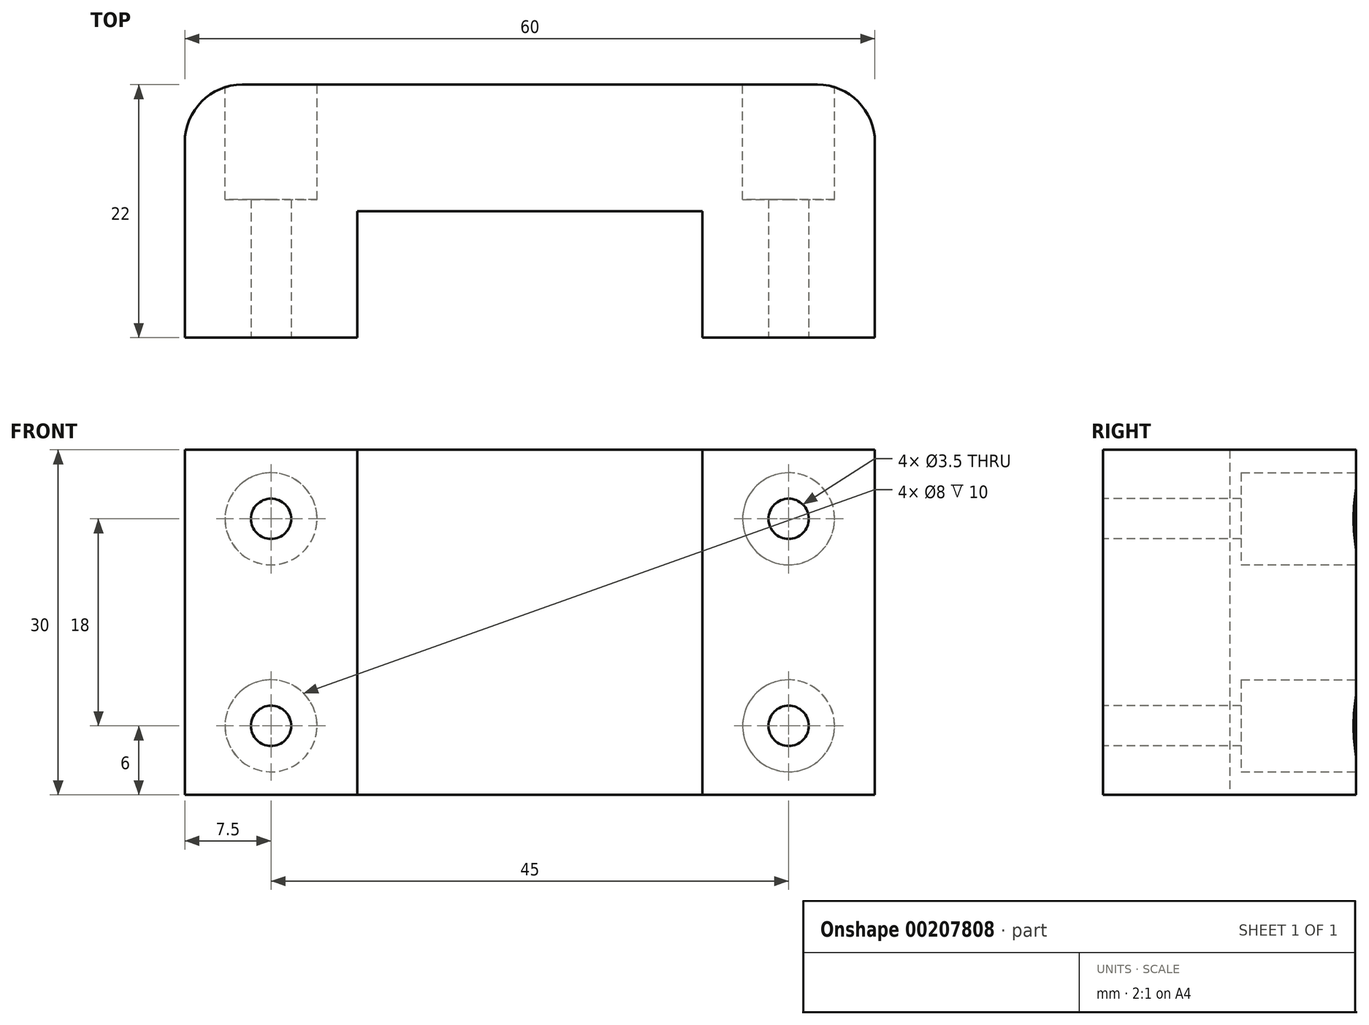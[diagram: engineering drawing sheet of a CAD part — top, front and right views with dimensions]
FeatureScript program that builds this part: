
annotation { "Feature Type Name" : "Feature", "Feature Type Description" : "" }
export const myFeature = defineFeature(function(context is Context, id is Id, definition is map)
    precondition{}
    {
        {
            var Q0;
            Q0=qCreatedBy(makeId("Top.planeOp"),FACE);
            var sketch = newSketch(context, id + "F0", { "sketchPlane" : qUnion([Q0])});
            skLineSegment(sketch, "E0.bottom", {"start": v(-25, 22) * mm, "end": v(25, 22) * mm});
            skLineSegment(sketch, "E0.top", {"start": v(-30, 0) * mm, "end": v(30, 0) * mm});
            skLineSegment(sketch, "E0.left", {"start": v(-30, 17) * mm, "end": v(-30, 0) * mm});
            skLineSegment(sketch, "E0.right", {"start": v(30, 17) * mm, "end": v(30, 0) * mm});
            skLineSegment(sketch, "E1.bottom", {"start": v(-15, 11) * mm, "end": v(15, 11) * mm});
            skLineSegment(sketch, "E1.top", {"start": v(-15, -2) * mm, "end": v(15, -2) * mm});
            skLineSegment(sketch, "E1.left", {"start": v(-15, 11) * mm, "end": v(-15, -2) * mm});
            skLineSegment(sketch, "E1.right", {"start": v(15, 11) * mm, "end": v(15, -2) * mm});
            skPoint(sketch, "E2.visualSharp", {"position": v(30, 22) * mm});
            skArc(sketch, "E2.filletArc", {"start": v(30, 17) * mm, "mid": v(28.54, 20.54) * mm, "end": v(25, 22) * mm});
            skPoint(sketch, "E3.visualSharp", {"position": v(-30, 22) * mm});
            skArc(sketch, "E3.filletArc", {"start": v(-25, 22) * mm, "mid": v(-28.54, 20.54) * mm, "end": v(-30, 17) * mm});
            skSolve(sketch);
        }
        {
            var Q0;
            Q0=makeQuery(id+"F0.imprint","IMPRINT",FACE,{"disambiguationData":[TD([[makeQuery(id+"F0.imprint","IMPRINT",EDGE,{"derivedFrom":sQuery(id+"F0.wireOp",EDGE,"E0.bottom")}),-1.0]])]});
            extrude(context, id + "F1", {"entities" : qUnion([Q0]), "depth" : 30 * mm});
        }
        {
            var Q0;
            {var subQ0=sQuery(id+"F0.wireOp",EDGE,"E0.top");Q0=makeQuery(id+"F1.opExtrude","SWEPT_FACE",FACE,{"disambiguationData":[OSD([subQ0]),TDD([makeQuery(id+"F0.imprint","IMPRINT",EDGE,{"disambiguationData":[TD([[makeQuery(id+"F0.imprint","INTERSECT",VERTEX,{"derivedFrom":[subQ0,sQuery(id+"F0.wireOp",EDGE,"E0.left")]}),-1.0]])],"derivedFrom":subQ0})])]});}
            var sketch = newSketch(context, id + "F2", { "sketchPlane" : qUnion([Q0])});
            skCircle(sketch, "E4", {"center": v(-22.5, 24) * mm, "radius": 1.75 * mm});
            skCircle(sketch, "E5", {"center": v(-22.5, 6) * mm, "radius": 1.75 * mm});
            skSolve(sketch);
        }
        {
            var Q0;
            {var subQ0=sQuery(id+"F0.wireOp",EDGE,"E0.top");Q0=makeQuery(id+"F1.opExtrude","SWEPT_FACE",FACE,{"disambiguationData":[OSD([subQ0]),TDD([makeQuery(id+"F0.imprint","IMPRINT",EDGE,{"disambiguationData":[TD([[makeQuery(id+"F0.imprint","INTERSECT",VERTEX,{"derivedFrom":[subQ0,sQuery(id+"F0.wireOp",EDGE,"E0.right")]}),1.0]])],"derivedFrom":subQ0})])]});}
            var sketch = newSketch(context, id + "F3", { "sketchPlane" : qUnion([Q0])});
            skCircle(sketch, "E6", {"center": v(22.5, 24) * mm, "radius": 1.75 * mm});
            skCircle(sketch, "E7", {"center": v(22.5, 6) * mm, "radius": 1.75 * mm});
            skSolve(sketch);
        }
        {
            var Q0;
            Q0=makeQuery(id+"F2.imprint","IMPRINT",FACE,{"disambiguationData":[TD([[makeQuery(id+"F2.imprint","IMPRINT",EDGE,{"derivedFrom":sQuery(id+"F2.wireOp",EDGE,"E4")}),1.0]])]});
            var Q1;
            Q1=makeQuery(id+"F2.imprint","IMPRINT",FACE,{"disambiguationData":[TD([[makeQuery(id+"F2.imprint","IMPRINT",EDGE,{"derivedFrom":sQuery(id+"F2.wireOp",EDGE,"E5")}),1.0]])]});
            var Q2;
            Q2=makeQuery(id+"F3.imprint","IMPRINT",FACE,{"disambiguationData":[TD([[makeQuery(id+"F3.imprint","IMPRINT",EDGE,{"derivedFrom":sQuery(id+"F3.wireOp",EDGE,"E7")}),1.0]])]});
            var Q3;
            Q3=makeQuery(id+"F3.imprint","IMPRINT",FACE,{"disambiguationData":[TD([[makeQuery(id+"F3.imprint","IMPRINT",EDGE,{"derivedFrom":sQuery(id+"F3.wireOp",EDGE,"E6")}),1.0]])]});
            extrude(context, id + "F4", {"entities" : qUnion([Q0, Q1, Q2, Q3]), "operationType" : NewBodyOperationType.REMOVE, "endBound" : BoundingType.THROUGH_ALL, "oppositeDirection" : true, "depth" : 25 * mm});
        }
        {
            var Q0;
            Q0=makeQuery(id+"F1.opExtrude","SWEPT_FACE",FACE,{"disambiguationData":[OSD([sQuery(id+"F0.wireOp",EDGE,"E0.bottom")])]});
            var sketch = newSketch(context, id + "F5", { "sketchPlane" : qUnion([Q0])});
            skCircle(sketch, "E8", {"center": v(22.5, 24) * mm, "radius": 4 * mm});
            skCircle(sketch, "E9", {"center": v(22.5, 6) * mm, "radius": 4 * mm});
            skCircle(sketch, "E10", {"center": v(-22.5, 24) * mm, "radius": 4 * mm});
            skCircle(sketch, "E11", {"center": v(-22.5, 6) * mm, "radius": 4 * mm});
            skSolve(sketch);
        }
        {
            var Q0;
            {var subQ0=sQuery(id+"F5.wireOp",EDGE,"E8");var subQ1=makeQuery(id+"F1.opExtrude","SWEPT_EDGE",EDGE,{"disambiguationData":[OSD([sQuery(id+"F0.wireOp",EDGE,"E0.bottom"),sQuery(id+"F0.wireOp",EDGE,"E3.filletArc")])]});var subQ2=makeQuery(id+"F5.imprint","INTERSECT",VERTEX,{"disambiguationData":[OD(0.0)],"derivedFrom":[subQ1,subQ0]});Q0=makeQuery(id+"F5.imprint","IMPRINT",FACE,{"disambiguationData":[TD([[makeQuery(id+"F5.imprint","IMPRINT",EDGE,{"disambiguationData":[TD([[subQ2,1.0]])],"derivedFrom":subQ0}),1.0]])]});}
            var Q1;
            {var subQ1=sQuery(id+"F0.wireOp",EDGE,"E0.bottom");Q1=makeQuery(id+"F5.imprint","IMPRINT",FACE,{"disambiguationData":[TD([[makeQuery(id+"F5.imprint","IMPRINT",EDGE,{"derivedFrom":makeQuery(id+"F4.boolean.opBoolean","INTERSECT",EDGE,{"derivedFrom":[makeQuery(id+"F1.opExtrude","SWEPT_FACE",FACE,{"disambiguationData":[OSD([subQ1])]}),makeQuery(id+"F4.opExtrude","SWEPT_FACE",FACE,{"disambiguationData":[OSD([sQuery(id+"F2.wireOp",EDGE,"E4")])]})]})}),-1.0]])]});}
            var Q2;
            {var subQ1=sQuery(id+"F0.wireOp",EDGE,"E0.bottom");Q2=makeQuery(id+"F5.imprint","IMPRINT",FACE,{"disambiguationData":[TD([[makeQuery(id+"F5.imprint","IMPRINT",EDGE,{"derivedFrom":makeQuery(id+"F4.boolean.opBoolean","INTERSECT",EDGE,{"derivedFrom":[makeQuery(id+"F1.opExtrude","SWEPT_FACE",FACE,{"disambiguationData":[OSD([subQ1])]}),makeQuery(id+"F4.opExtrude","SWEPT_FACE",FACE,{"disambiguationData":[OSD([sQuery(id+"F2.wireOp",EDGE,"E5")])]})]})}),-1.0]])]});}
            var Q3;
            {var subQ0=sQuery(id+"F5.wireOp",EDGE,"E9");var subQ1=makeQuery(id+"F1.opExtrude","SWEPT_EDGE",EDGE,{"disambiguationData":[OSD([sQuery(id+"F0.wireOp",EDGE,"E0.bottom"),sQuery(id+"F0.wireOp",EDGE,"E3.filletArc")])]});var subQ2=makeQuery(id+"F5.imprint","INTERSECT",VERTEX,{"disambiguationData":[OD(0.0)],"derivedFrom":[subQ1,subQ0]});Q3=makeQuery(id+"F5.imprint","IMPRINT",FACE,{"disambiguationData":[TD([[makeQuery(id+"F5.imprint","IMPRINT",EDGE,{"disambiguationData":[TD([[subQ2,-1.0]])],"derivedFrom":subQ0}),1.0]])]});}
            var Q4;
            {var subQ1=sQuery(id+"F0.wireOp",EDGE,"E0.bottom");Q4=makeQuery(id+"F5.imprint","IMPRINT",FACE,{"disambiguationData":[TD([[makeQuery(id+"F5.imprint","IMPRINT",EDGE,{"derivedFrom":makeQuery(id+"F4.boolean.opBoolean","INTERSECT",EDGE,{"derivedFrom":[makeQuery(id+"F1.opExtrude","SWEPT_FACE",FACE,{"disambiguationData":[OSD([subQ1])]}),makeQuery(id+"F4.opExtrude","SWEPT_FACE",FACE,{"disambiguationData":[OSD([sQuery(id+"F3.wireOp",EDGE,"E7")])]})]})}),-1.0]])]});}
            var Q5;
            {var subQ0=sQuery(id+"F5.wireOp",EDGE,"E11");var subQ1=makeQuery(id+"F1.opExtrude","SWEPT_EDGE",EDGE,{"disambiguationData":[OSD([sQuery(id+"F0.wireOp",EDGE,"E0.bottom"),sQuery(id+"F0.wireOp",EDGE,"E2.filletArc")])]});var subQ2=makeQuery(id+"F5.imprint","INTERSECT",VERTEX,{"disambiguationData":[OD(0.0)],"derivedFrom":[subQ1,subQ0]});Q5=makeQuery(id+"F5.imprint","IMPRINT",FACE,{"disambiguationData":[TD([[makeQuery(id+"F5.imprint","IMPRINT",EDGE,{"disambiguationData":[TD([[subQ2,1.0]])],"derivedFrom":subQ0}),1.0]])]});}
            var Q6;
            {var subQ1=sQuery(id+"F0.wireOp",EDGE,"E0.bottom");Q6=makeQuery(id+"F5.imprint","IMPRINT",FACE,{"disambiguationData":[TD([[makeQuery(id+"F5.imprint","IMPRINT",EDGE,{"derivedFrom":makeQuery(id+"F4.boolean.opBoolean","INTERSECT",EDGE,{"derivedFrom":[makeQuery(id+"F1.opExtrude","SWEPT_FACE",FACE,{"disambiguationData":[OSD([subQ1])]}),makeQuery(id+"F4.opExtrude","SWEPT_FACE",FACE,{"disambiguationData":[OSD([sQuery(id+"F3.wireOp",EDGE,"E6")])]})]})}),-1.0]])]});}
            var Q7;
            {var subQ0=sQuery(id+"F5.wireOp",EDGE,"E10");var subQ1=makeQuery(id+"F1.opExtrude","SWEPT_EDGE",EDGE,{"disambiguationData":[OSD([sQuery(id+"F0.wireOp",EDGE,"E0.bottom"),sQuery(id+"F0.wireOp",EDGE,"E2.filletArc")])]});var subQ2=makeQuery(id+"F5.imprint","INTERSECT",VERTEX,{"disambiguationData":[OD(0.0)],"derivedFrom":[subQ1,subQ0]});Q7=makeQuery(id+"F5.imprint","IMPRINT",FACE,{"disambiguationData":[TD([[makeQuery(id+"F5.imprint","IMPRINT",EDGE,{"disambiguationData":[TD([[subQ2,-1.0]])],"derivedFrom":subQ0}),1.0]])]});}
            extrude(context, id + "F6", {"entities" : qUnion([Q0, Q1, Q2, Q3, Q4, Q5, Q6, Q7]), "operationType" : NewBodyOperationType.REMOVE, "oppositeDirection" : true, "depth" : 10 * mm});
        }
    });
